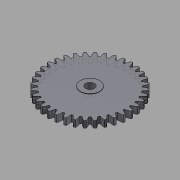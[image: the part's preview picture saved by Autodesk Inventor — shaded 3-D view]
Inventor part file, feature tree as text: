
AUTODESK INVENTOR PART (.ipt)
format: ipt  version: 2015 (Build 190159000, 159)  size: 325,632 bytes
history: native  units: in
note: dims shown in document units (in); Inventor stores cm internally (conversion verified against a paired STEP export)
features: other x13, sketch x4, plane x2
ambient origin geometry x8: Origin, YZ Plane, XZ Plane, XY Plane, X Axis, Y Axis, Z Axis, Center Point
bodies: Solid1 (feature_tree)
feature tree (19):
  other  "Spur Gear27_MIR3.ipt"
  other  "Solid1::Spur Gear27_MIR3.ipt"
  other  "TaggingFeature1"
  sketch  "Sketch1"  dims[d0=0.3937in]
  sketch  "Sketch2"  dims[d16=0.4528in d17=0.0in d41=0.0in d43=0.4528in d46=0.4528in d47=0.0in d48=0.0in]
  sketch  "Sketch3"
  sketch  "Sketch4"
  plane  "XZ Plane_1"
  plane  "Work Plane2"
  other  "Z Axis_1"
  other  "Srf1"
  other  "Srf1::Derived"
  other  "Distance iMate"
  other  "Align iMate"
  other  "Mesh iMate"
  other  "Axis iMate"
  other  "Position iMate"
  other  "Mesh iMate2"
  other  "Start plane iMate"
